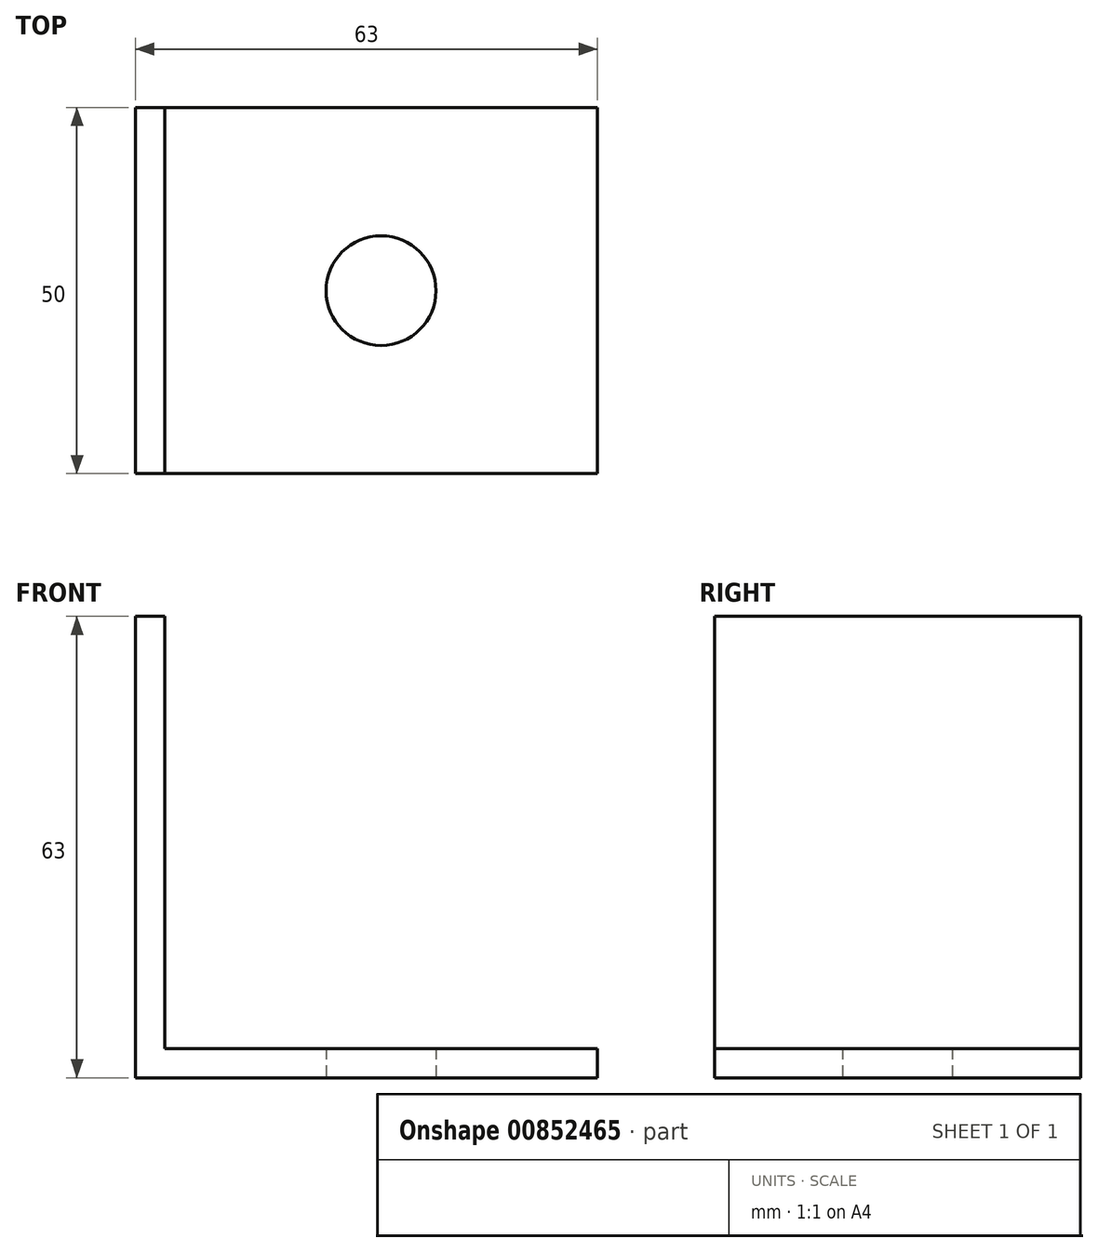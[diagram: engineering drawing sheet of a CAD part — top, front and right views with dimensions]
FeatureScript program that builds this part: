
annotation { "Feature Type Name" : "Feature", "Feature Type Description" : "" }
export const myFeature = defineFeature(function(context is Context, id is Id, definition is map)
    precondition{}
    {
        {
            var Q0;
            Q0=qCreatedBy(makeId("Top.planeOp"),FACE);
            var sketch = newSketch(context, id + "F0", { "sketchPlane" : qUnion([Q0])});
            skLineSegment(sketch, "E0.bottom", {"start": v(-29.5, 25) * mm, "end": v(29.5, 25) * mm});
            skLineSegment(sketch, "E0.top", {"start": v(-29.5, -25) * mm, "end": v(29.5, -25) * mm});
            skLineSegment(sketch, "E0.left", {"start": v(-29.5, 25) * mm, "end": v(-29.5, -25) * mm});
            skLineSegment(sketch, "E0.right", {"start": v(29.5, 25) * mm, "end": v(29.5, -25) * mm});
            skPoint(sketch, "E0.middle", {"position": v(0, 0) * mm});
            skCircle(sketch, "E1", {"center": v(0, 0) * mm, "radius": 7.5 * mm});
            skLineSegment(sketch, "E2.bottom", {"start": v(29.5, 25) * mm, "end": v(33.5, 25) * mm});
            skLineSegment(sketch, "E2.top", {"start": v(29.5, -25) * mm, "end": v(33.5, -25) * mm});
            skLineSegment(sketch, "E2.right", {"start": v(33.5, 25) * mm, "end": v(33.5, -25) * mm});
            skSolve(sketch);
        }
        {
            var Q0;
            Q0=makeQuery(id+"F0.imprint","IMPRINT",FACE,{"disambiguationData":[TD([[makeQuery(id+"F0.imprint","IMPRINT",EDGE,{"derivedFrom":sQuery(id+"F0.wireOp",EDGE,"E0.bottom")}),-1.0]])]});
            extrude(context, id + "F1", {"entities" : qUnion([Q0]), "depth" : 4 * mm, "offsetDistance" : 25 * mm});
        }
        {
            var Q0;
            Q0=makeQuery(id+"F1.opExtrude","CAP_FACE",FACE,{"disambiguationData":[OSD([sQuery(id+"F0.wireOp",EDGE,"E0.bottom"),sQuery(id+"F0.wireOp",EDGE,"E0.top"),sQuery(id+"F0.wireOp",EDGE,"E0.left"),sQuery(id+"F0.wireOp",EDGE,"E1"),sQuery(id+"F0.wireOp",EDGE,"E0.right")])],"isStart":true});
            var sketch = newSketch(context, id + "F2", { "sketchPlane" : qUnion([Q0])});
            skLineSegment(sketch, "E3.bottom", {"start": v(-29.5, -25) * mm, "end": v(-33.5, -25) * mm});
            skLineSegment(sketch, "E3.top", {"start": v(-29.5, 25) * mm, "end": v(-33.5, 25) * mm});
            skLineSegment(sketch, "E3.left", {"start": v(-29.5, -25) * mm, "end": v(-29.5, 25) * mm});
            skLineSegment(sketch, "E3.right", {"start": v(-33.5, -25) * mm, "end": v(-33.5, 25) * mm});
            skSolve(sketch);
        }
        {
            var Q0;
            Q0 = qSketchRegion(id + "F2", true);
            extrude(context, id + "F3", {"entities" : qUnion([Q0]), "operationType" : NewBodyOperationType.ADD, "oppositeDirection" : true, "depth" : 63 * mm, "offsetDistance" : 25 * mm});
        }
    });
